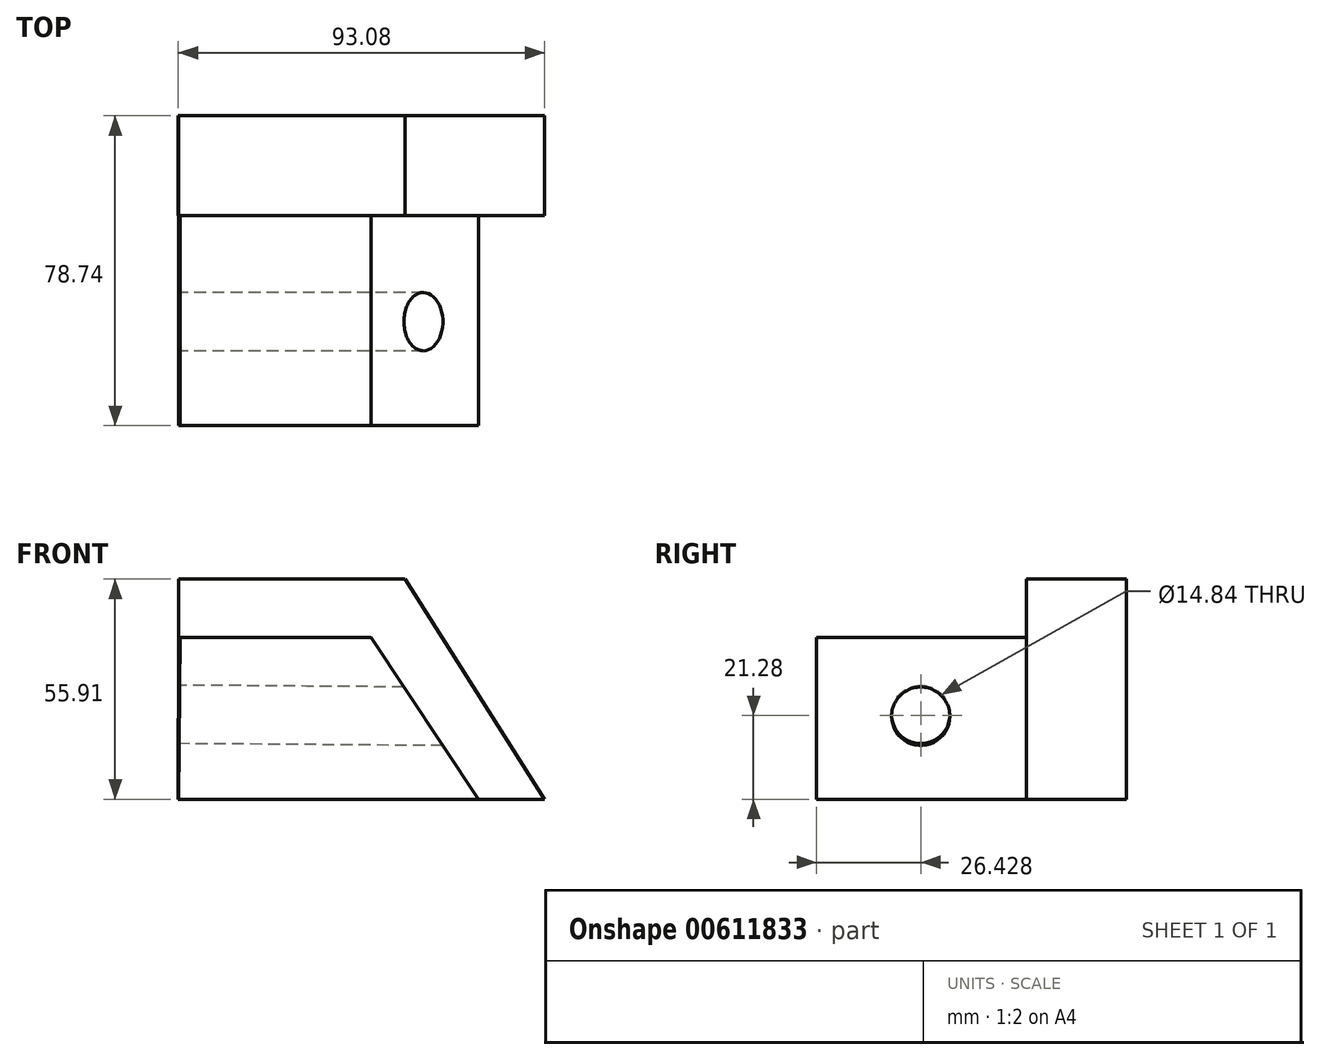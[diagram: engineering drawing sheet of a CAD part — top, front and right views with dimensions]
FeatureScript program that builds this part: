
annotation { "Feature Type Name" : "Feature", "Feature Type Description" : "" }
export const myFeature = defineFeature(function(context is Context, id is Id, definition is map)
    precondition{}
    {
        {
            var Q0;
            Q0=qCreatedBy(makeId("Front.planeOp"),FACE);
            var sketch = newSketch(context, id + "F0", { "sketchPlane" : qUnion([Q0])});
            skLineSegment(sketch, "E0", {"start": v(0, 0) * mm, "end": v(-27.33, 41.07) * mm});
            skLineSegment(sketch, "E1", {"start": v(-27.33, 41.07) * mm, "end": v(-75.89, 41.07) * mm});
            skLineSegment(sketch, "E2", {"start": v(0, 0) * mm, "end": v(-76.2, 0) * mm});
            skLineSegment(sketch, "E3", {"start": v(-76.2, 0) * mm, "end": v(-75.89, 41.07) * mm});
            skSolve(sketch);
        }
        {
            var Q0;
            Q0 = qSketchRegion(id + "F0", true);
            extrude(context, id + "F1", {"entities" : qUnion([Q0]), "depth" : 68.58 * mm, "offsetDistance" : 25.4 * mm});
        }
        {
            var Q0;
            Q0=qCreatedBy(makeId("Front.planeOp"),FACE);
            var sketch = newSketch(context, id + "F2", { "sketchPlane" : qUnion([Q0])});
            skLineSegment(sketch, "E4", {"start": v(-76.23, 55.9) * mm, "end": v(-18.74, 55.9) * mm});
            skLineSegment(sketch, "E5", {"start": v(-18.74, 55.9) * mm, "end": v(16.77, 0) * mm});
            skLineSegment(sketch, "E6", {"start": v(16.77, 0) * mm, "end": v(0, 0) * mm});
            skLineSegment(sketch, "E7", {"start": v(-76.23, 55.9) * mm, "end": v(-76.23, 41.24) * mm});
            skLineSegment(sketch, "E8", {"start": v(0, 0) * mm, "end": v(-76.3, 0) * mm});
            skLineSegment(sketch, "E9", {"start": v(-76.3, 0) * mm, "end": v(-76.23, 41.24) * mm});
            skSolve(sketch);
        }
        {
            var Q0;
            Q0 = qSketchRegion(id + "F2", true);
            extrude(context, id + "F3", {"entities" : qUnion([Q0]), "operationType" : NewBodyOperationType.ADD, "depth" : 25.4 * mm, "offsetDistance" : 25.4 * mm});
        }
        {
            var Q0;
            Q0=makeQuery(id+"F1.opExtrude","CAP_FACE",FACE,{"disambiguationData":[OSD([sQuery(id+"F0.wireOp",EDGE,"E0"),sQuery(id+"F0.wireOp",EDGE,"E1"),sQuery(id+"F0.wireOp",EDGE,"E2"),sQuery(id+"F0.wireOp",EDGE,"E3")])],"isStart":false});
            extrude(context, id + "F4", {"entities" : qUnion([Q0]), "operationType" : NewBodyOperationType.ADD, "depth" : 10.16 * mm, "offsetDistance" : 25.4 * mm});
        }
        {
            var Q0;
            {var subQ0=sQuery(id+"F0.wireOp",EDGE,"E3");Q0=makeQuery(id+"F4.boolean.opBoolean","MERGE",FACE,{"derivedFrom":[makeQuery(id+"F1.opExtrude","SWEPT_FACE",FACE,{"disambiguationData":[OSD([subQ0])]}),makeQuery(id+"F4.opExtrude","SWEPT_FACE",FACE,{"disambiguationData":[OSD([subQ0])]})]});}
            var sketch = newSketch(context, id + "F5", { "sketchPlane" : qUnion([Q0])});
            skCircle(sketch, "E10", {"center": v(52.31, 20.97) * mm, "radius": 7.42 * mm});
            skSolve(sketch);
        }
        {
            var Q0;
            Q0=makeQuery(id+"F5.imprint","IMPRINT",FACE,{"disambiguationData":[TD([[makeQuery(id+"F5.imprint","IMPRINT",EDGE,{"derivedFrom":sQuery(id+"F5.wireOp",EDGE,"E10")}),1.0]])]});
            extrude(context, id + "F6", {"entities" : qUnion([Q0]), "operationType" : NewBodyOperationType.REMOVE, "oppositeDirection" : true, "depth" : 127 * mm, "offsetDistance" : 25.4 * mm});
        }
    });
